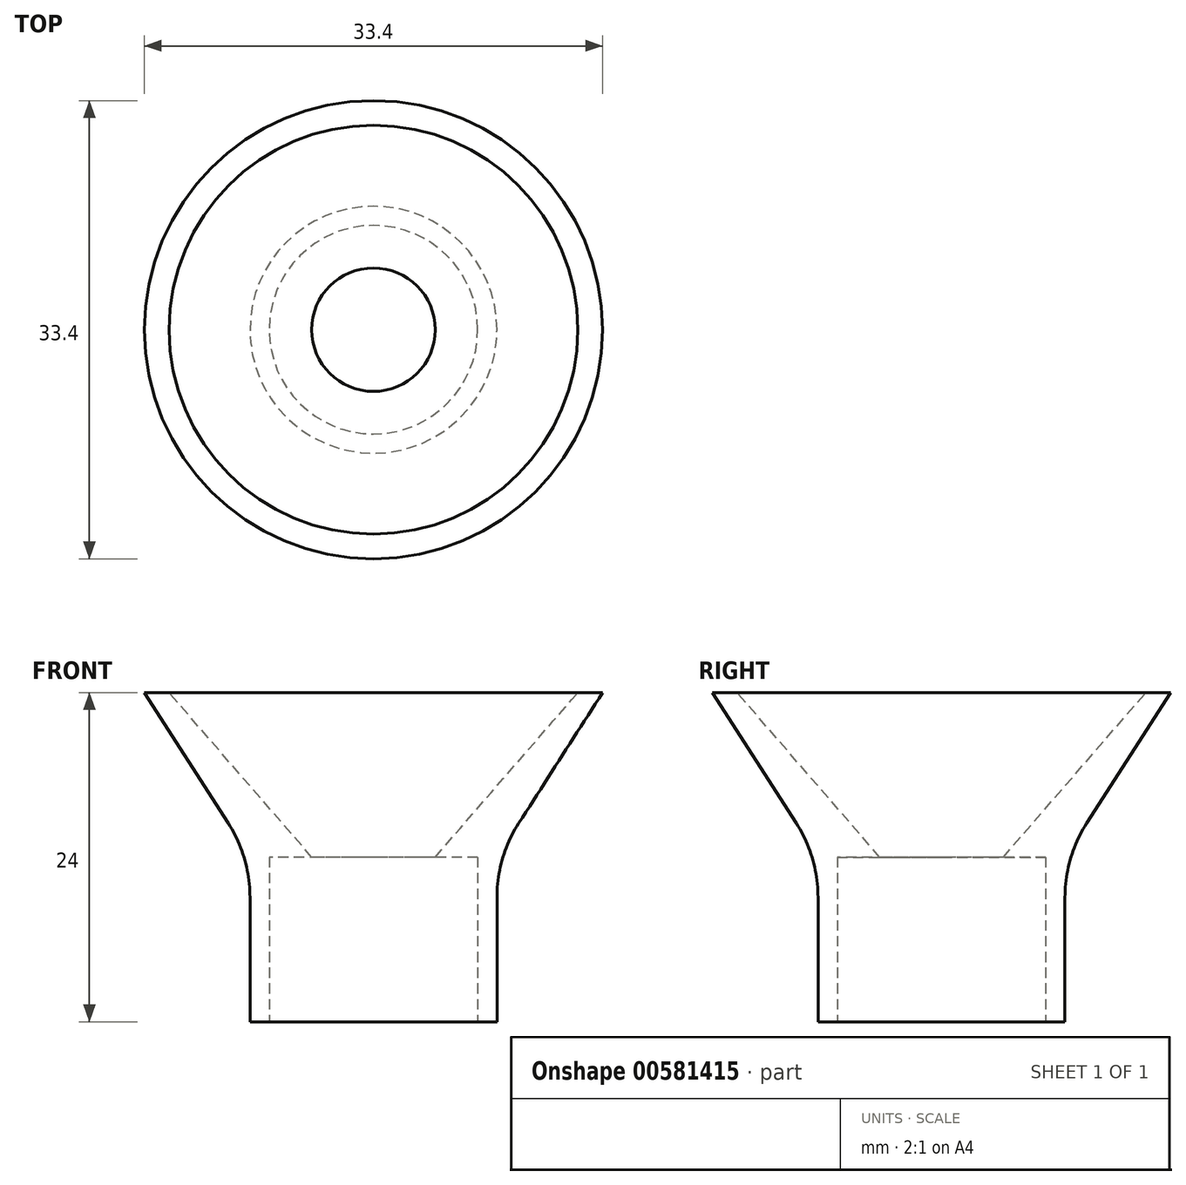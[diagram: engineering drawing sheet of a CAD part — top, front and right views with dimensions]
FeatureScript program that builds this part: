
annotation { "Feature Type Name" : "Feature", "Feature Type Description" : "" }
export const myFeature = defineFeature(function(context is Context, id is Id, definition is map)
    precondition{}
    {
        {
            var Q0;
            Q0=qCreatedBy(makeId("Top.planeOp"),FACE);
            var sketch = newSketch(context, id + "F0", { "sketchPlane" : qUnion([Q0])});
            skCircle(sketch, "E0", {"center": v(0, 0) * mm, "radius": 7.6 * mm});
            skCircle(sketch, "E1", {"center": v(0, 0) * mm, "radius": 9 * mm});
            skSolve(sketch);
        }
        {
            var Q0;
            Q0=qCreatedBy(makeId("Front.planeOp"),FACE);
            var sketch = newSketch(context, id + "F1", { "sketchPlane" : qUnion([Q0])});
            skLineSegment(sketch, "E2", {"start": v(0, 12) * mm, "end": v(4.5, 12) * mm});
            skLineSegment(sketch, "E3", {"start": v(4.5, 12) * mm, "end": v(9, 12) * mm});
            skLineSegment(sketch, "E4", {"start": v(4.5, 12) * mm, "end": v(14.9, 24) * mm});
            skLineSegment(sketch, "E5", {"start": v(14.9, 24) * mm, "end": v(16.7, 24) * mm});
            skLineSegment(sketch, "E6", {"start": v(9, 12) * mm, "end": v(16.7, 24) * mm});
            skSolve(sketch);
        }
        {
            var Q0;
            Q0=qCreatedBy(makeId("Front.planeOp"),FACE);
            var sketch = newSketch(context, id + "F2", { "sketchPlane" : qUnion([Q0])});
            skLineSegment(sketch, "E7", {"start": v(0, 14.21) * mm, "end": v(0, -26.25) * mm, "construction": true});
            skSolve(sketch);
        }
        {
            var Q0;
            Q0 = qSketchRegion(id + "F0", true);
            extrude(context, id + "F3", {"entities" : qUnion([Q0]), "depth" : 12 * mm, "offsetDistance" : 25 * mm});
        }
        {
            var Q0;
            Q0=makeQuery(id+"F1.imprint","IMPRINT",FACE,{"disambiguationData":[TD([[makeQuery(id+"F1.imprint","IMPRINT",EDGE,{"derivedFrom":sQuery(id+"F1.wireOp",EDGE,"e0ffb129-e06f-46e2-ae6d-2dcbf39bb2d2")}),-1.0]])]});
            var Q1;
            Q1=makeQuery(id+"F1.imprint","IMPRINT",FACE,{"disambiguationData":[TD([[makeQuery(id+"F1.imprint","IMPRINT",EDGE,{"derivedFrom":sQuery(id+"F1.wireOp",EDGE,"E3")}),1.0]])]});
            var Q2;
            Q2=sQuery(id+"F2.wireOp",EDGE,"E7");
            revolve(context, id + "F4", {"operationType" : NewBodyOperationType.ADD, "entities" : qUnion([Q0, Q1]), "axis" : qUnion([Q2]), "revolveType" : RevolveType.FULL});
        }
        {
            var Q0;
            Q0=makeQuery(id+"F4.boolean.opBoolean","MERGE",EDGE,{"derivedFrom":[makeQuery(id+"F3.opExtrude","CAP_EDGE",EDGE,{"disambiguationData":[OSD([sQuery(id+"F0.wireOp",EDGE,"E1")])],"isStart":false}),makeQuery(id+"F4.opRevolve","SWEPT_EDGE",EDGE,{"disambiguationData":[OSD([sQuery(id+"F1.wireOp",EDGE,"E3"),sQuery(id+"F1.wireOp",EDGE,"ac94bc2b-24bb-464d-80a0-044655c09be9")])]})]});
            fillet(context, id + "F5", {"entities" : qUnion([Q0]), "radius" : 10 * mm, "tangentPropagation" : true, "allowEdgeOverflow" : false});
        }
    });
